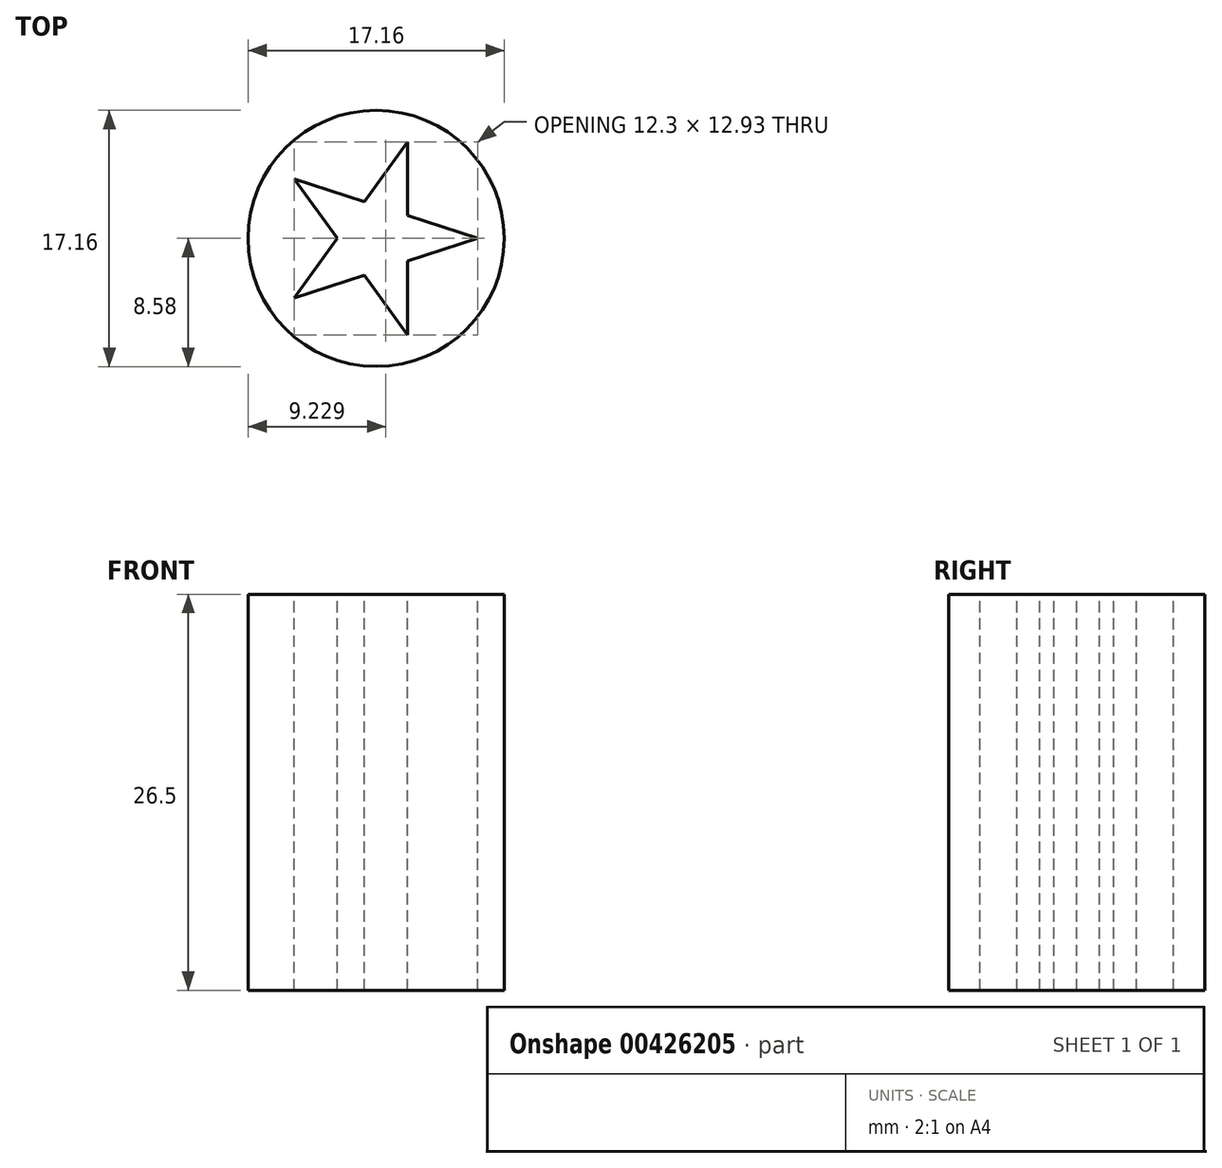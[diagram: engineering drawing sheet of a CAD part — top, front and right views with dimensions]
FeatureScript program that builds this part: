
annotation { "Feature Type Name" : "Feature", "Feature Type Description" : "" }
export const myFeature = defineFeature(function(context is Context, id is Id, definition is map)
    precondition{}
    {
        {
            var Q0;
            Q0=qCreatedBy(makeId("Top.planeOp"),FACE);
            var sketch = newSketch(context, id + "F0", { "sketchPlane" : qUnion([Q0])});
            skCircle(sketch, "E0", {"center": v(0, 0) * mm, "radius": 8.57 * mm});
            skSolve(sketch);
        }
        {
            var Q0;
            Q0=makeQuery(id+"F0.imprint","IMPRINT",FACE,{"disambiguationData":[TD([[makeQuery(id+"F0.imprint","IMPRINT",EDGE,{"derivedFrom":sQuery(id+"F0.wireOp",EDGE,"E0")}),1.0]])]});
            extrude(context, id + "F1", {"entities" : qUnion([Q0]), "depth" : 26.5 * mm});
        }
        {
            var Q0;
            Q0=makeQuery(id+"F1.opExtrude","CAP_FACE",FACE,{"disambiguationData":[OSD([sQuery(id+"F0.wireOp",EDGE,"E0")])],"isStart":false});
            var sketch = newSketch(context, id + "F2", { "sketchPlane" : qUnion([Q0])});
            skCircle(sketch, "E1.cCircle", {"center": v(0, 0) * mm, "radius": 5.5 * mm, "construction": true});
            skLineSegment(sketch, "E1.0", {"start": v(-5.5, -4) * mm, "end": v(-5.5, 4) * mm, "construction": true});
            skLineSegment(sketch, "E1.1", {"start": v(-5.5, 4) * mm, "end": v(2.1, 6.47) * mm, "construction": true});
            skLineSegment(sketch, "E1.2", {"start": v(2.1, 6.47) * mm, "end": v(6.8, 0) * mm, "construction": true});
            skLineSegment(sketch, "E1.3", {"start": v(6.8, 0) * mm, "end": v(2.1, -6.47) * mm, "construction": true});
            skLineSegment(sketch, "E1.4", {"start": v(2.1, -6.47) * mm, "end": v(-5.5, -4) * mm, "construction": true});
            skPoint(sketch, "E1.0.midPoint", {"position": v(-5.5, 0) * mm});
            skLineSegment(sketch, "E2", {"start": v(-5.5, 4) * mm, "end": v(2.1, -6.47) * mm});
            skLineSegment(sketch, "E3", {"start": v(-5.5, -4) * mm, "end": v(6.8, 0) * mm});
            skLineSegment(sketch, "E4", {"start": v(2.1, 6.47) * mm, "end": v(-5.5, -4) * mm});
            skLineSegment(sketch, "E5", {"start": v(2.1, -6.47) * mm, "end": v(2.1, 6.47) * mm});
            skLineSegment(sketch, "E6", {"start": v(-5.5, 4) * mm, "end": v(6.8, 0) * mm});
            skSolve(sketch);
        }
        {
            var Q0;
            {var subQ0=sQuery(id+"F2.wireOp",EDGE,"E6");var subQ1=sQuery(id+"F2.wireOp",EDGE,"E2");var subQ2=makeQuery(id+"F2.imprint","INTERSECT",VERTEX,{"derivedFrom":[subQ1,subQ0]});Q0=makeQuery(id+"F2.imprint","IMPRINT",FACE,{"disambiguationData":[TD([[makeQuery(id+"F2.imprint","IMPRINT",EDGE,{"disambiguationData":[TD([[subQ2,-1.0]])],"derivedFrom":subQ1}),1.0]])]});}
            var Q1;
            {var subQ0=sQuery(id+"F2.wireOp",EDGE,"E5");var subQ1=sQuery(id+"F2.wireOp",EDGE,"E4");var subQ2=makeQuery(id+"F2.imprint","INTERSECT",VERTEX,{"derivedFrom":[subQ1,subQ0]});Q1=makeQuery(id+"F2.imprint","IMPRINT",FACE,{"disambiguationData":[TD([[makeQuery(id+"F2.imprint","IMPRINT",EDGE,{"disambiguationData":[TD([[subQ2,-1.0]])],"derivedFrom":subQ1}),1.0]])]});}
            var Q2;
            {var subQ5=sQuery(id+"F2.wireOp",EDGE,"E4");var subQ6=sQuery(id+"F2.wireOp",EDGE,"E2");var subQ7=makeQuery(id+"F2.imprint","INTERSECT",VERTEX,{"derivedFrom":[subQ6,subQ5]});Q2=makeQuery(id+"F2.imprint","IMPRINT",FACE,{"disambiguationData":[TD([[makeQuery(id+"F2.imprint","IMPRINT",EDGE,{"disambiguationData":[TD([[subQ7,-1.0]])],"derivedFrom":subQ6}),1.0]])]});}
            var Q3;
            {var subQ0=sQuery(id+"F2.wireOp",EDGE,"E4");var subQ1=sQuery(id+"F2.wireOp",EDGE,"E2");var subQ2=makeQuery(id+"F2.imprint","INTERSECT",VERTEX,{"derivedFrom":[subQ1,subQ0]});Q3=makeQuery(id+"F2.imprint","IMPRINT",FACE,{"disambiguationData":[TD([[makeQuery(id+"F2.imprint","IMPRINT",EDGE,{"disambiguationData":[TD([[subQ2,-1.0]])],"derivedFrom":subQ1}),-1.0]])]});}
            var Q4;
            {var subQ0=sQuery(id+"F2.wireOp",EDGE,"E5");var subQ1=sQuery(id+"F2.wireOp",EDGE,"E2");var subQ2=makeQuery(id+"F2.imprint","INTERSECT",VERTEX,{"derivedFrom":[subQ1,subQ0]});Q4=makeQuery(id+"F2.imprint","IMPRINT",FACE,{"disambiguationData":[TD([[makeQuery(id+"F2.imprint","IMPRINT",EDGE,{"disambiguationData":[TD([[subQ2,1.0]])],"derivedFrom":subQ1}),1.0]])]});}
            var Q5;
            {var subQ0=sQuery(id+"F2.wireOp",EDGE,"E6");var subQ1=sQuery(id+"F2.wireOp",EDGE,"E3");var subQ2=makeQuery(id+"F2.imprint","INTERSECT",VERTEX,{"derivedFrom":[subQ1,subQ0]});Q5=makeQuery(id+"F2.imprint","IMPRINT",FACE,{"disambiguationData":[TD([[makeQuery(id+"F2.imprint","IMPRINT",EDGE,{"disambiguationData":[TD([[subQ2,1.0]])],"derivedFrom":subQ1}),1.0]])]});}
            extrude(context, id + "F3", {"entities" : qUnion([Q0, Q1, Q2, Q3, Q4, Q5]), "operationType" : NewBodyOperationType.REMOVE, "oppositeDirection" : true, "depth" : 26.5 * mm});
        }
    });
